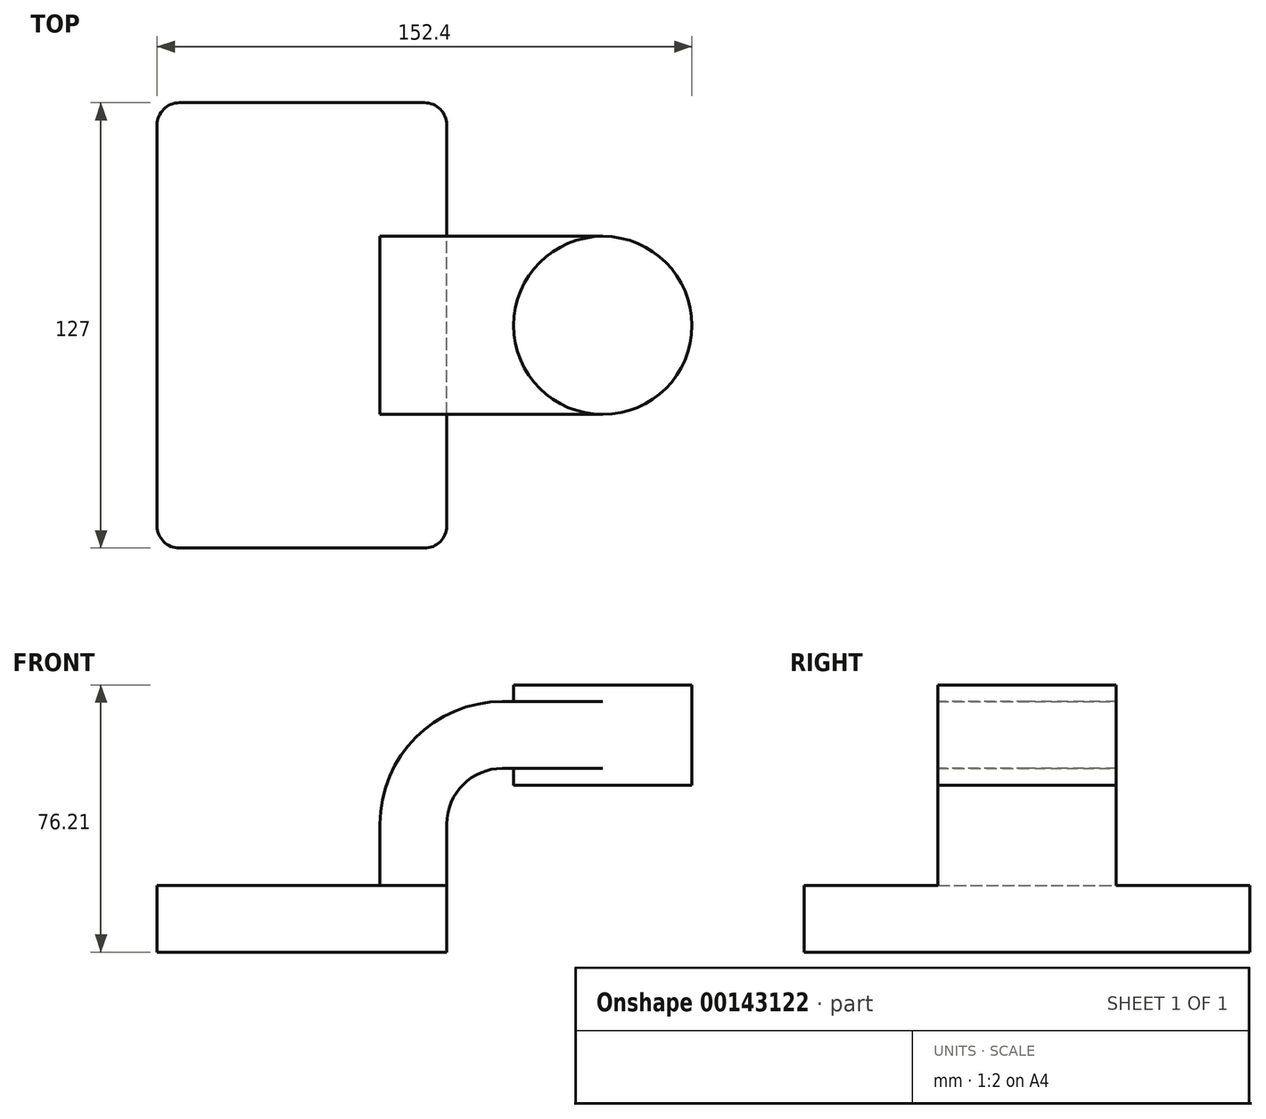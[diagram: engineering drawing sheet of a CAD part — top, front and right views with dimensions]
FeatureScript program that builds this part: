
annotation { "Feature Type Name" : "Feature", "Feature Type Description" : "" }
export const myFeature = defineFeature(function(context is Context, id is Id, definition is map)
    precondition{}
    {
        {
            var Q0;
            Q0=qCreatedBy(makeId("Front.planeOp"),FACE);
            var sketch = newSketch(context, id + "F0", { "sketchPlane" : qUnion([Q0])});
            skLineSegment(sketch, "E0.bottom", {"start": v(-41.28, 9.52) * mm, "end": v(41.27, 9.53) * mm});
            skLineSegment(sketch, "E0.top", {"start": v(-41.28, -9.53) * mm, "end": v(41.28, -9.53) * mm});
            skLineSegment(sketch, "E0.left", {"start": v(-41.28, 9.52) * mm, "end": v(-41.28, -9.53) * mm});
            skLineSegment(sketch, "E0.right", {"start": v(41.27, 9.53) * mm, "end": v(41.28, -9.52) * mm});
            skPoint(sketch, "E0.middle", {"position": v(0, 0) * mm});
            skLineSegment(sketch, "E1", {"start": v(41.27, 9.53) * mm, "end": v(41.27, 27) * mm});
            skArc(sketch, "E2", {"start": v(41.27, 27) * mm, "mid": v(45.92, 38.23) * mm, "end": v(57.15, 42.88) * mm});
            skLineSegment(sketch, "E3.bottom", {"start": v(60.32, 38.1) * mm, "end": v(111.13, 38.1) * mm});
            skLineSegment(sketch, "E3.top", {"start": v(60.32, 66.68) * mm, "end": v(111.12, 66.68) * mm});
            skLineSegment(sketch, "E3.left", {"start": v(60.32, 38.1) * mm, "end": v(60.32, 66.67) * mm});
            skLineSegment(sketch, "E3.right", {"start": v(111.13, 38.1) * mm, "end": v(111.12, 66.67) * mm});
            skPoint(sketch, "E3.middle", {"position": v(85.72, 52.39) * mm});
            skLineSegment(sketch, "E4", {"start": v(57.15, 42.88) * mm, "end": v(85.72, 42.88) * mm});
            skLineSegment(sketch, "E5.0", {"start": v(57.15, 61.93) * mm, "end": v(85.72, 61.93) * mm});
            skArc(sketch, "E5.1", {"start": v(22.22, 27) * mm, "mid": v(32.45, 51.7) * mm, "end": v(57.15, 61.93) * mm});
            skLineSegment(sketch, "E5.2", {"start": v(22.22, 9.53) * mm, "end": v(22.22, 27) * mm});
            skLineSegment(sketch, "E6", {"start": v(85.72, 38.1) * mm, "end": v(85.72, 66.68) * mm});
            skFitSpline(sketch, "E7", {"points": [v(-41.28, 9.52) * mm, v(57.15, 61.93) * mm], "startDerivative": vector(0, 85.72) * mm, "endDerivative": vector(95.64, 0) * mm});
            skSolve(sketch);
        }
        {
            var Q0;
            Q0=makeQuery(id+"F0.imprint","IMPRINT",FACE,{"disambiguationData":[TD([[makeQuery(id+"F0.imprint","IMPRINT",EDGE,{"derivedFrom":sQuery(id+"F0.wireOp",EDGE,"E0.top")}),1.0]])]});
            extrude(context, id + "F1", {"entities" : qUnion([Q0]), "endBound" : BoundingType.SYMMETRIC, "depth" : 127 * mm});
        }
        {
            var Q0;
            {var subQ5=sQuery(id+"F0.wireOp",EDGE,"E1");Q0=makeQuery(id+"F0.imprint","IMPRINT",FACE,{"disambiguationData":[TD([[makeQuery(id+"F0.imprint","IMPRINT",EDGE,{"derivedFrom":subQ5}),1.0]])]});}
            var Q1;
            {var subQ0=sQuery(id+"F0.wireOp",EDGE,"E4");var subQ1=sQuery(id+"F0.wireOp",EDGE,"E3.left");var subQ2=makeQuery(id+"F0.imprint","INTERSECT",VERTEX,{"derivedFrom":[subQ1,subQ0]});Q1=makeQuery(id+"F0.imprint","IMPRINT",FACE,{"disambiguationData":[TD([[makeQuery(id+"F0.imprint","IMPRINT",EDGE,{"disambiguationData":[TD([[subQ2,-1.0]])],"derivedFrom":subQ1}),-1.0]])]});}
            extrude(context, id + "F2", {"entities" : qUnion([Q0, Q1]), "operationType" : NewBodyOperationType.ADD, "endBound" : BoundingType.SYMMETRIC, "depth" : 50.8 * mm});
        }
        {
            var Q0;
            Q0=makeQuery(id+"F0.imprint","IMPRINT",FACE,{"disambiguationData":[TD([[makeQuery(id+"F0.imprint","IMPRINT",EDGE,{"derivedFrom":sQuery(id+"F0.wireOp",EDGE,"E5.1")}),1.0]])]});
            extrude(context, id + "F3", {"entities" : qUnion([Q0]), "operationType" : NewBodyOperationType.ADD, "endBound" : BoundingType.SYMMETRIC, "depth" : 15.88 * mm});
        }
        {
            var Q0;
            {var subQ4=sQuery(id+"F0.wireOp",EDGE,"E3.right");Q0=makeQuery(id+"F0.imprint","IMPRINT",FACE,{"disambiguationData":[TD([[makeQuery(id+"F0.imprint","IMPRINT",EDGE,{"derivedFrom":subQ4}),1.0]])]});}
            var Q1;
            Q1=sQuery(id+"F0.wireOp",EDGE,"E6");
            revolve(context, id + "F4", {"operationType" : NewBodyOperationType.ADD, "entities" : qUnion([Q0]), "axis" : qUnion([Q1]), "revolveType" : RevolveType.FULL});
        }
        {
            var Q0;
            Q0=makeQuery(id+"F1.opExtrude","CAP_EDGE",EDGE,{"disambiguationData":[OSD([sQuery(id+"F0.wireOp",EDGE,"E0.right")])],"isStart":false});
            var Q1;
            Q1=makeQuery(id+"F1.opExtrude","CAP_EDGE",EDGE,{"disambiguationData":[OSD([sQuery(id+"F0.wireOp",EDGE,"E0.left")])],"isStart":false});
            var Q2;
            Q2=makeQuery(id+"F1.opExtrude","CAP_EDGE",EDGE,{"disambiguationData":[OSD([sQuery(id+"F0.wireOp",EDGE,"E0.right")])],"isStart":true});
            var Q3;
            Q3=makeQuery(id+"F1.opExtrude","CAP_EDGE",EDGE,{"disambiguationData":[OSD([sQuery(id+"F0.wireOp",EDGE,"E0.left")])],"isStart":true});
            fillet(context, id + "F5", {"entities" : qUnion([Q0, Q1, Q2, Q3]), "radius" : 6.35 * mm, "tangentPropagation" : true, "allowEdgeOverflow" : false});
        }
    });
